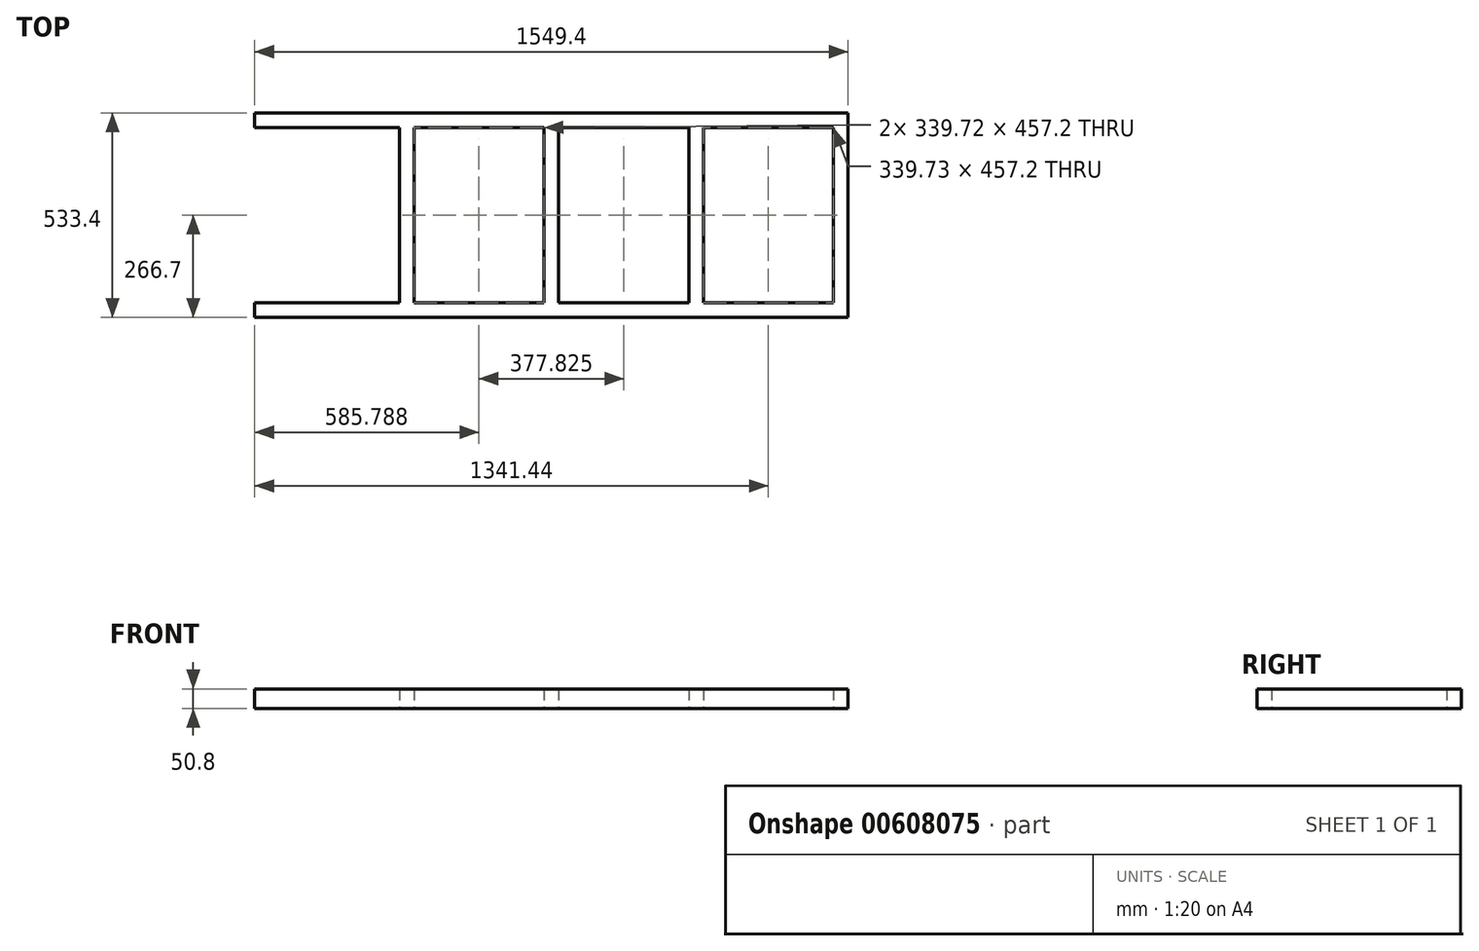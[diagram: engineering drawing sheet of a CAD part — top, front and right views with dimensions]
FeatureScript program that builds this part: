
annotation { "Feature Type Name" : "Feature", "Feature Type Description" : "" }
export const myFeature = defineFeature(function(context is Context, id is Id, definition is map)
    precondition{}
    {
        {
            var Q0;
            Q0=qCreatedBy(makeId("Top.planeOp"),FACE);
            var sketch = newSketch(context, id + "F0", { "sketchPlane" : qUnion([Q0])});
            skLineSegment(sketch, "E0.bottom", {"start": v(-850.9, 330.2) * mm, "end": v(850.9, 330.2) * mm, "construction": true});
            skLineSegment(sketch, "E0.top", {"start": v(-850.9, -330.2) * mm, "end": v(850.9, -330.2) * mm, "construction": true});
            skLineSegment(sketch, "E0.left", {"start": v(-850.9, 330.2) * mm, "end": v(-850.9, -330.2) * mm, "construction": true});
            skLineSegment(sketch, "E0.right", {"start": v(850.9, 330.2) * mm, "end": v(850.9, -330.2) * mm, "construction": true});
            skLineSegment(sketch, "E1.bottom", {"start": v(-850.9, 292.1) * mm, "end": v(850.9, 292.1) * mm, "construction": true});
            skLineSegment(sketch, "E1.left", {"start": v(-850.9, 292.1) * mm, "end": v(-850.9, 330.2) * mm, "construction": true});
            skLineSegment(sketch, "E1.right", {"start": v(850.9, 292.1) * mm, "end": v(850.9, 330.2) * mm, "construction": true});
            skLineSegment(sketch, "E2.bottom", {"start": v(812.8, 292.1) * mm, "end": v(850.9, 292.1) * mm, "construction": true});
            skLineSegment(sketch, "E2.top", {"start": v(812.8, -330.2) * mm, "end": v(850.9, -330.2) * mm, "construction": true});
            skLineSegment(sketch, "E2.left", {"start": v(812.8, 292.1) * mm, "end": v(812.8, -330.2) * mm, "construction": true});
            skLineSegment(sketch, "E2.right", {"start": v(850.9, 292.1) * mm, "end": v(850.9, -330.2) * mm, "construction": true});
            skLineSegment(sketch, "E3.bottom", {"start": v(-774.7, -241.3) * mm, "end": v(774.7, -241.3) * mm});
            skLineSegment(sketch, "E3.top", {"start": v(-774.7, -279.4) * mm, "end": v(774.7, -279.4) * mm});
            skLineSegment(sketch, "E3.left", {"start": v(-774.7, -241.3) * mm, "end": v(-774.7, -279.4) * mm});
            skLineSegment(sketch, "E3.right", {"start": v(774.7, -241.3) * mm, "end": v(774.7, -279.4) * mm});
            skLineSegment(sketch, "E4.bottom", {"start": v(-774.7, 254) * mm, "end": v(774.7, 254) * mm});
            skLineSegment(sketch, "E4.top", {"start": v(-774.7, 215.9) * mm, "end": v(774.7, 215.9) * mm});
            skLineSegment(sketch, "E4.left", {"start": v(-774.7, 254) * mm, "end": v(-774.7, 215.9) * mm});
            skLineSegment(sketch, "E4.right", {"start": v(774.7, 254) * mm, "end": v(774.7, 215.9) * mm});
            skSolve(sketch);
        }
        {
            var Q0;
            Q0=makeQuery(id+"F0.imprint","IMPRINT",FACE,{"disambiguationData":[TD([[makeQuery(id+"F0.imprint","IMPRINT",EDGE,{"derivedFrom":sQuery(id+"F0.wireOp",EDGE,"E4.bottom")}),-1.0]])]});
            var Q1;
            Q1=makeQuery(id+"F0.imprint","IMPRINT",FACE,{"disambiguationData":[TD([[makeQuery(id+"F0.imprint","IMPRINT",EDGE,{"derivedFrom":sQuery(id+"F0.wireOp",EDGE,"E3.bottom")}),-1.0]])]});
            extrude(context, id + "F1", {"entities" : qUnion([Q0, Q1]), "depth" : 50.8 * mm, "offsetDistance" : 25.4 * mm});
        }
        {
            var Q0;
            Q0=qCreatedBy(makeId("Top.planeOp"),FACE);
            var sketch = newSketch(context, id + "F2", { "sketchPlane" : qUnion([Q0])});
            skLineSegment(sketch, "E5.bottom", {"start": v(-850.9, 330.2) * mm, "end": v(850.9, 330.2) * mm, "construction": true});
            skLineSegment(sketch, "E5.top", {"start": v(-850.9, -330.2) * mm, "end": v(850.9, -330.2) * mm, "construction": true});
            skLineSegment(sketch, "E5.left", {"start": v(-850.9, 330.2) * mm, "end": v(-850.9, -330.2) * mm, "construction": true});
            skLineSegment(sketch, "E5.right", {"start": v(850.9, 330.2) * mm, "end": v(850.9, -330.2) * mm, "construction": true});
            skLineSegment(sketch, "E6.bottom", {"start": v(-850.9, 292.1) * mm, "end": v(850.9, 292.1) * mm, "construction": true});
            skLineSegment(sketch, "E6.left", {"start": v(-850.9, 292.1) * mm, "end": v(-850.9, 330.2) * mm, "construction": true});
            skLineSegment(sketch, "E6.right", {"start": v(850.9, 292.1) * mm, "end": v(850.9, 330.2) * mm, "construction": true});
            skLineSegment(sketch, "E7.bottom", {"start": v(812.8, 292.1) * mm, "end": v(850.9, 292.1) * mm, "construction": true});
            skLineSegment(sketch, "E7.top", {"start": v(812.8, -330.2) * mm, "end": v(850.9, -330.2) * mm, "construction": true});
            skLineSegment(sketch, "E7.left", {"start": v(812.8, 292.1) * mm, "end": v(812.8, -330.2) * mm, "construction": true});
            skLineSegment(sketch, "E7.right", {"start": v(850.9, 292.1) * mm, "end": v(850.9, -330.2) * mm, "construction": true});
            skLineSegment(sketch, "E8.bottom", {"start": v(-774.7, -241.3) * mm, "end": v(774.7, -241.3) * mm});
            skLineSegment(sketch, "E8.top", {"start": v(-774.7, -279.4) * mm, "end": v(774.7, -279.4) * mm});
            skLineSegment(sketch, "E8.left", {"start": v(-774.7, -241.3) * mm, "end": v(-774.7, -279.4) * mm});
            skLineSegment(sketch, "E8.right", {"start": v(774.7, -241.3) * mm, "end": v(774.7, -279.4) * mm});
            skLineSegment(sketch, "E9.bottom", {"start": v(-774.7, 254) * mm, "end": v(774.7, 254) * mm});
            skLineSegment(sketch, "E9.top", {"start": v(-774.7, 215.9) * mm, "end": v(774.7, 215.9) * mm});
            skLineSegment(sketch, "E9.left", {"start": v(-774.7, 254) * mm, "end": v(-774.7, 215.9) * mm});
            skLineSegment(sketch, "E9.right", {"start": v(774.7, 254) * mm, "end": v(774.7, 215.9) * mm});
            skLineSegment(sketch, "E10.bottom", {"start": v(-774.7, 215.9) * mm, "end": v(-736.6, 215.9) * mm});
            skLineSegment(sketch, "E10.top", {"start": v(-774.7, -241.3) * mm, "end": v(-736.6, -241.3) * mm});
            skLineSegment(sketch, "E10.left", {"start": v(-774.7, 215.9) * mm, "end": v(-774.7, -241.3) * mm});
            skLineSegment(sketch, "E10.right", {"start": v(-736.6, 215.9) * mm, "end": v(-736.6, -241.3) * mm});
            skLineSegment(sketch, "E11.1.0.0", {"start": v(-358.78, 215.9) * mm, "end": v(-358.78, -241.3) * mm});
            skLineSegment(sketch, "E11.1.0.1", {"start": v(-396.88, 215.9) * mm, "end": v(-396.88, -241.3) * mm});
            skLineSegment(sketch, "E11.1.0.2", {"start": v(-396.88, -241.3) * mm, "end": v(-358.78, -241.3) * mm});
            skLineSegment(sketch, "E11.2.0.0", {"start": v(19.05, 215.9) * mm, "end": v(19.05, -241.3) * mm});
            skLineSegment(sketch, "E11.2.0.1", {"start": v(-19.05, 215.9) * mm, "end": v(-19.05, -241.3) * mm});
            skLineSegment(sketch, "E11.2.0.2", {"start": v(-19.05, -241.3) * mm, "end": v(19.05, -241.3) * mm});
            skLineSegment(sketch, "E11.3.0.0", {"start": v(396.88, 215.9) * mm, "end": v(396.88, -241.3) * mm});
            skLineSegment(sketch, "E11.3.0.1", {"start": v(358.77, 215.9) * mm, "end": v(358.77, -241.3) * mm});
            skLineSegment(sketch, "E11.3.0.2", {"start": v(358.77, -241.3) * mm, "end": v(396.88, -241.3) * mm});
            skLineSegment(sketch, "E11.4.0.0", {"start": v(774.7, 215.9) * mm, "end": v(774.7, -241.3) * mm});
            skLineSegment(sketch, "E11.4.0.1", {"start": v(736.6, 215.9) * mm, "end": v(736.6, -241.3) * mm});
            skLineSegment(sketch, "E11.4.0.2", {"start": v(736.6, -241.3) * mm, "end": v(774.7, -241.3) * mm});
            skLineSegment(sketch, "E11.direction1", {"start": v(-774.7, -241.3) * mm, "end": v(-396.88, -241.3) * mm, "construction": true});
            skSolve(sketch);
        }
        {
            var Q0;
            Q0=makeQuery(id+"F2.imprint","IMPRINT",FACE,{"disambiguationData":[TD([[makeQuery(id+"F2.imprint","IMPRINT",EDGE,{"derivedFrom":sQuery(id+"F2.wireOp",EDGE,"E10.bottom")}),-1.0]])]});
            var Q1;
            {var subQ0=sQuery(id+"F2.wireOp",EDGE,"E11.1.0.0");Q1=makeQuery(id+"F2.imprint","IMPRINT",FACE,{"disambiguationData":[TD([[makeQuery(id+"F2.imprint","IMPRINT",EDGE,{"derivedFrom":subQ0}),-1.0]])]});}
            var Q2;
            {var subQ0=sQuery(id+"F2.wireOp",EDGE,"E11.2.0.0");Q2=makeQuery(id+"F2.imprint","IMPRINT",FACE,{"disambiguationData":[TD([[makeQuery(id+"F2.imprint","IMPRINT",EDGE,{"derivedFrom":subQ0}),-1.0]])]});}
            var Q3;
            {var subQ0=sQuery(id+"F2.wireOp",EDGE,"E11.3.0.0");Q3=makeQuery(id+"F2.imprint","IMPRINT",FACE,{"disambiguationData":[TD([[makeQuery(id+"F2.imprint","IMPRINT",EDGE,{"derivedFrom":subQ0}),-1.0]])]});}
            var Q4;
            {var subQ0=sQuery(id+"F2.wireOp",EDGE,"E11.4.0.0");Q4=makeQuery(id+"F2.imprint","IMPRINT",FACE,{"disambiguationData":[TD([[makeQuery(id+"F2.imprint","IMPRINT",EDGE,{"derivedFrom":subQ0}),-1.0]])]});}
            var Q5;
            Q5=makeQuery(id+"F1.opExtrude","CAP_FACE",FACE,{"disambiguationData":[OSD([sQuery(id+"F0.wireOp",EDGE,"E4.bottom"),sQuery(id+"F0.wireOp",EDGE,"E4.top"),sQuery(id+"F0.wireOp",EDGE,"E4.left"),sQuery(id+"F0.wireOp",EDGE,"E4.right")])],"isStart":false});
            extrude(context, id + "F3", {"entities" : qUnion([Q0, Q1, Q2, Q3, Q4]), "operationType" : NewBodyOperationType.ADD, "endBound" : BoundingType.UP_TO_SURFACE, "depth" : 25.4 * mm, "endBoundEntityFace" : qUnion([Q5]), "offsetDistance" : 25.4 * mm});
        }
    });
